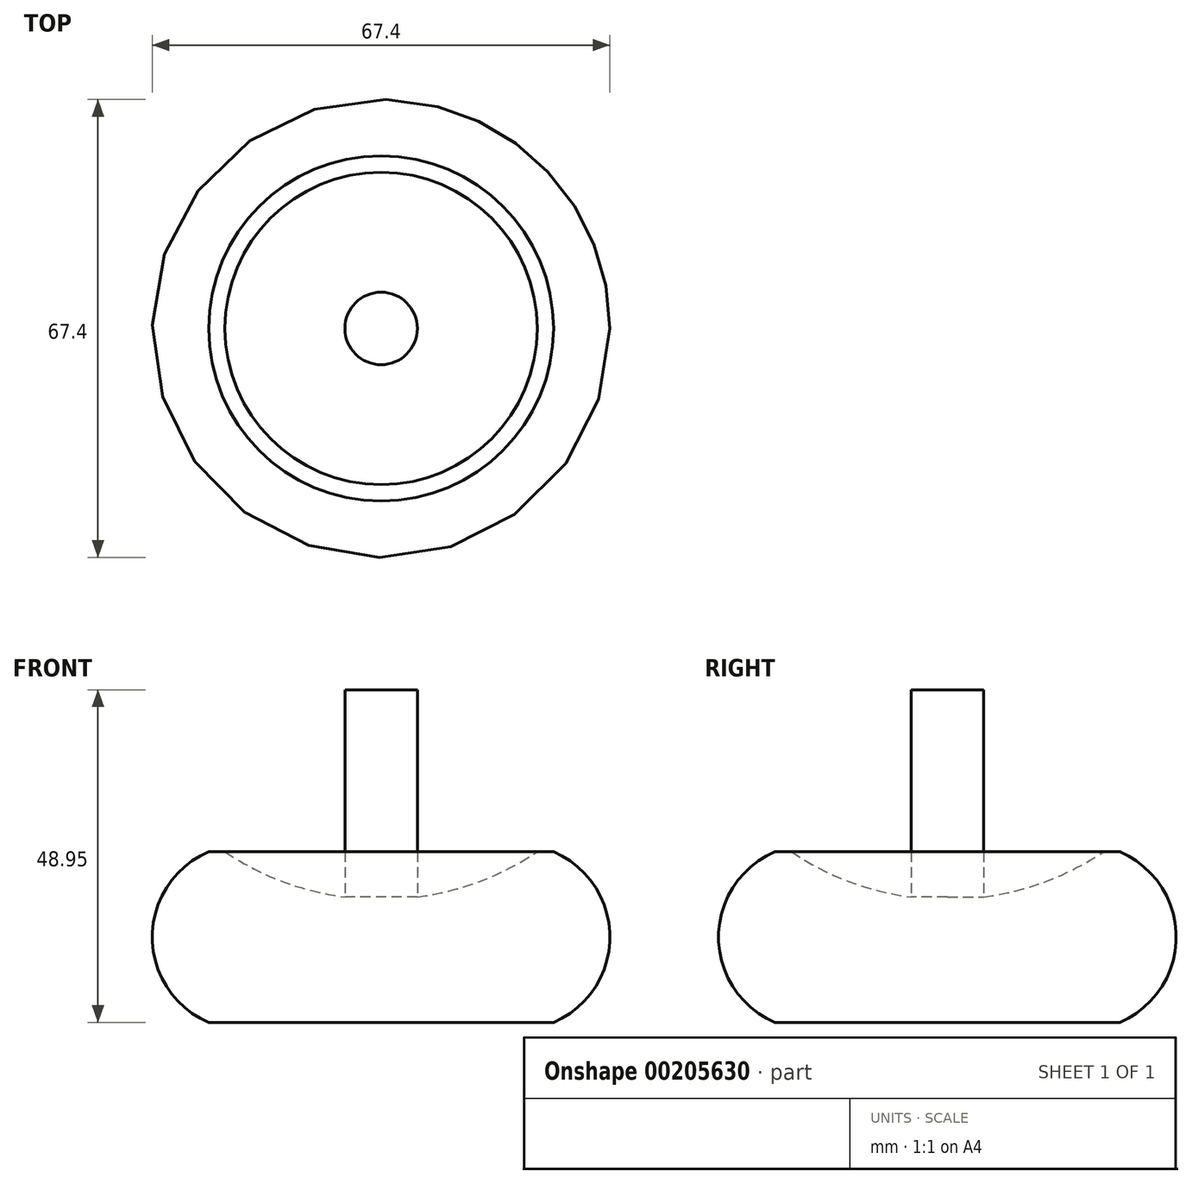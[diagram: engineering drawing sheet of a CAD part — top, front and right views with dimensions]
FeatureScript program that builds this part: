
annotation { "Feature Type Name" : "Feature", "Feature Type Description" : "" }
export const myFeature = defineFeature(function(context is Context, id is Id, definition is map)
    precondition{}
    {
        {
            var Q0;
            Q0=qCreatedBy(makeId("Front.planeOp"),FACE);
            var sketch = newSketch(context, id + "F0", { "sketchPlane" : qUnion([Q0])});
            skLineSegment(sketch, "E0", {"start": v(0, 15.04) * mm, "end": v(-25.4, 15.04) * mm});
            skLineSegment(sketch, "E1", {"start": v(0, -10.07) * mm, "end": v(-25.4, -10.07) * mm});
            skArc(sketch, "E2", {"start": v(-25.4, 15.04) * mm, "mid": v(-33.7, 2.48) * mm, "end": v(-25.4, -10.07) * mm});
            skLineSegment(sketch, "E3", {"start": v(0, 15.04) * mm, "end": v(0, -10.07) * mm});
            skSolve(sketch);
        }
        {
            var Q0;
            Q0=makeQuery(id+"F0.imprint","IMPRINT",FACE,{"disambiguationData":[TD([[makeQuery(id+"F0.imprint","IMPRINT",EDGE,{"derivedFrom":sQuery(id+"F0.wireOp",EDGE,"E0")}),1.0]])]});
            var Q1;
            Q1=sQuery(id+"F0.wireOp",EDGE,"E3");
            revolve(context, id + "F1", {"entities" : qUnion([Q0]), "axis" : qUnion([Q1]), "revolveType" : RevolveType.FULL});
        }
        {
            var Q0;
            Q0=qCreatedBy(makeId("Front.planeOp"),FACE);
            var sketch = newSketch(context, id + "F2", { "sketchPlane" : qUnion([Q0])});
            skArc(sketch, "E4", {"start": v(-23, 15.04) * mm, "mid": v(-12.02, 9.82) * mm, "end": v(0, 8.03) * mm});
            skLineSegment(sketch, "E5", {"start": v(-23, 15.04) * mm, "end": v(0, 15.04) * mm});
            skLineSegment(sketch, "E6", {"start": v(0, 15.04) * mm, "end": v(0, 8.03) * mm});
            skSolve(sketch);
        }
        {
            var Q0;
            Q0=makeQuery(id+"F2.imprint","IMPRINT",FACE,{"disambiguationData":[TD([[makeQuery(id+"F2.imprint","IMPRINT",EDGE,{"derivedFrom":sQuery(id+"F2.wireOp",EDGE,"E4")}),1.0]])]});
            var Q1;
            Q1=sQuery(id+"F2.wireOp",EDGE,"E6");
            revolve(context, id + "F3", {"operationType" : NewBodyOperationType.REMOVE, "entities" : qUnion([Q0]), "axis" : qUnion([Q1]), "revolveType" : RevolveType.FULL, "oppositeDirection" : true});
        }
        {
            var Q0;
            Q0=qCreatedBy(makeId("Front.planeOp"),FACE);
            var sketch = newSketch(context, id + "F4", { "sketchPlane" : qUnion([Q0])});
            skLineSegment(sketch, "E7.bottom", {"start": v(0, 0) * mm, "end": v(5.33, 0) * mm});
            skLineSegment(sketch, "E7.top", {"start": v(0, 38.88) * mm, "end": v(5.33, 38.88) * mm});
            skLineSegment(sketch, "E7.left", {"start": v(0, 0) * mm, "end": v(0, 38.88) * mm});
            skLineSegment(sketch, "E7.right", {"start": v(5.33, 0) * mm, "end": v(5.33, 38.88) * mm});
            skSolve(sketch);
        }
        {
            var Q0;
            Q0=makeQuery(id+"F4.imprint","IMPRINT",FACE,{"disambiguationData":[TD([[makeQuery(id+"F4.imprint","IMPRINT",EDGE,{"derivedFrom":sQuery(id+"F4.wireOp",EDGE,"E7.bottom")}),1.0]])]});
            var Q1;
            Q1=sQuery(id+"F4.wireOp",EDGE,"E7.left");
            revolve(context, id + "F5", {"operationType" : NewBodyOperationType.ADD, "entities" : qUnion([Q0]), "axis" : qUnion([Q1]), "revolveType" : RevolveType.FULL});
        }
    });
